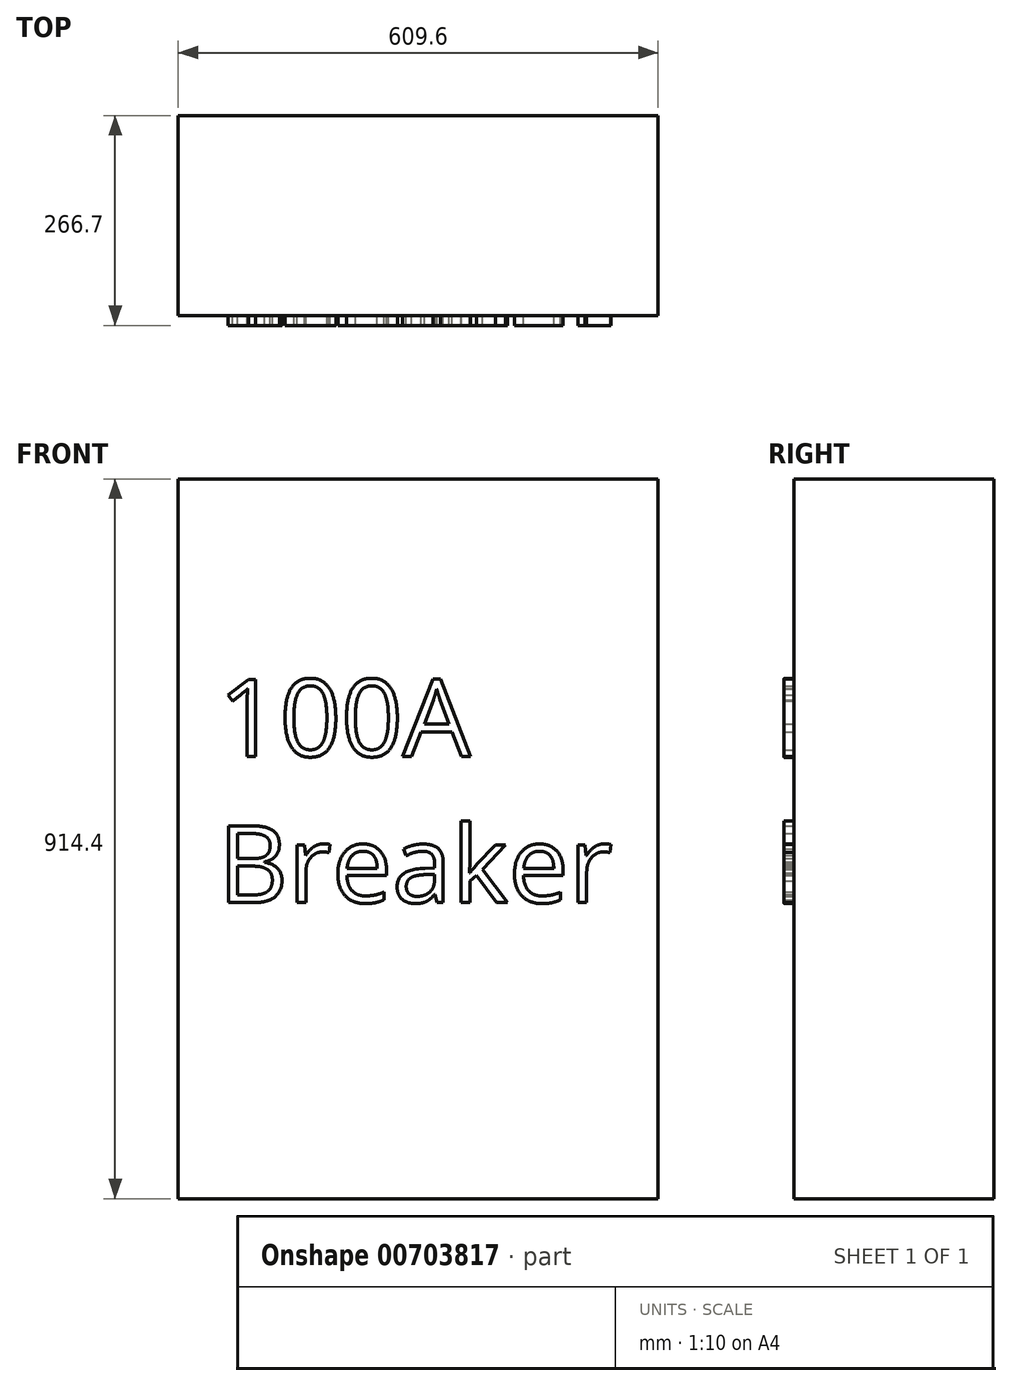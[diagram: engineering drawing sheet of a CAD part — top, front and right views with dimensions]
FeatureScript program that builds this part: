
annotation { "Feature Type Name" : "Feature", "Feature Type Description" : "" }
export const myFeature = defineFeature(function(context is Context, id is Id, definition is map)
    precondition{}
    {
        {
            var Q0;
            Q0=qCreatedBy(makeId("Front.planeOp"),FACE);
            var sketch = newSketch(context, id + "F0", { "sketchPlane" : qUnion([Q0])});
            skLineSegment(sketch, "E0.bottom", {"start": v(304.8, -457.2) * mm, "end": v(-304.8, -457.2) * mm});
            skLineSegment(sketch, "E0.top", {"start": v(304.8, 457.2) * mm, "end": v(-304.8, 457.2) * mm});
            skLineSegment(sketch, "E0.left", {"start": v(304.8, -457.2) * mm, "end": v(304.8, 457.2) * mm});
            skLineSegment(sketch, "E0.right", {"start": v(-304.8, -457.2) * mm, "end": v(-304.8, 457.2) * mm});
            skPoint(sketch, "E0.middle", {"position": v(0, 0) * mm});
            skSolve(sketch);
        }
        {
            var Q0;
            Q0=makeQuery(id+"F0.imprint","IMPRINT",FACE,{"disambiguationData":[TD([[makeQuery(id+"F0.imprint","IMPRINT",EDGE,{"derivedFrom":sQuery(id+"F0.wireOp",EDGE,"E0.bottom")}),-1.0]])]});
            extrude(context, id + "F1", {"entities" : qUnion([Q0]), "depth" : 254 * mm, "offsetDistance" : 25.4 * mm});
        }
        {
            var Q0;
            Q0=makeQuery(id+"F1.opExtrude","CAP_FACE",FACE,{"disambiguationData":[OSD([sQuery(id+"F0.wireOp",EDGE,"E0.bottom"),sQuery(id+"F0.wireOp",EDGE,"E0.top"),sQuery(id+"F0.wireOp",EDGE,"E0.left"),sQuery(id+"F0.wireOp",EDGE,"E0.right")])],"isStart":false});
            var sketch = newSketch(context, id + "F2", { "sketchPlane" : qUnion([Q0])});
            skText(sketch, "E1", { "text": "100A \nBreaker\n", "fontName": "OpenSans-Regular.ttf"});
            const initialGuessF2  = {"E1": [-0.254, 0.10483, 1, 0, 0.09837]};
            skSetInitialGuess(sketch, initialGuessF2);
            skSolve(sketch);
        }
        {
            var Q0;
            Q0 = qSketchRegion(id + "F2", true);
            extrude(context, id + "F3", {"entities" : qUnion([Q0]), "operationType" : NewBodyOperationType.ADD, "depth" : 12.7 * mm, "offsetDistance" : 25.4 * mm});
        }
    });
